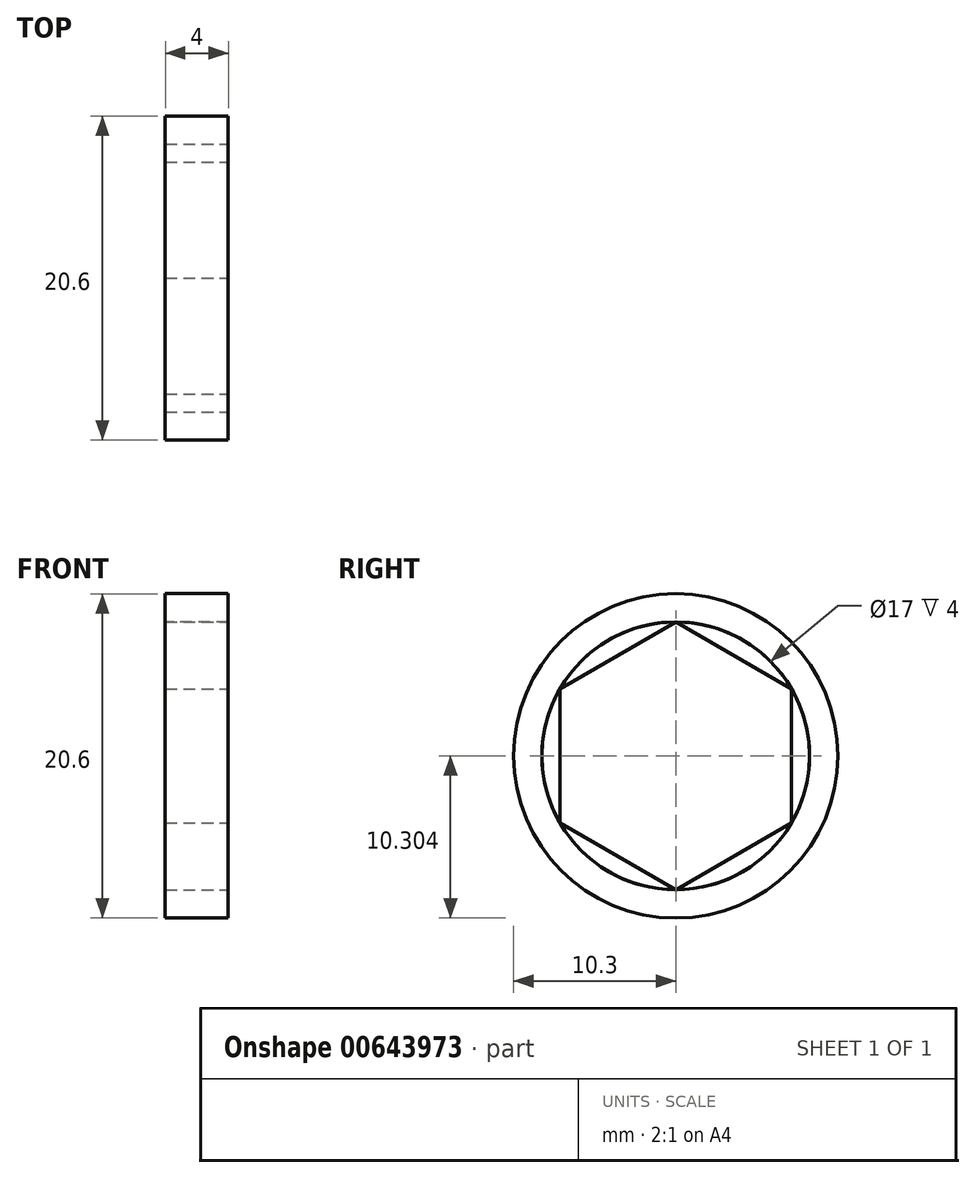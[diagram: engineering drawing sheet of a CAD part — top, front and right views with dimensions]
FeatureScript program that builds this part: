
annotation { "Feature Type Name" : "Feature", "Feature Type Description" : "" }
export const myFeature = defineFeature(function(context is Context, id is Id, definition is map)
    precondition{}
    {
        {
            var Q0;
            Q0=qCreatedBy(makeId("Front.planeOp"),FACE);
            var sketch = newSketch(context, id + "F0", { "sketchPlane" : qUnion([Q0])});
            skLineSegment(sketch, "E0.bottom", {"start": v(-21.35, 23.47) * mm, "end": v(-17.35, 23.47) * mm});
            skLineSegment(sketch, "E0.top", {"start": v(-21.35, 21.67) * mm, "end": v(-17.35, 21.67) * mm});
            skLineSegment(sketch, "E0.left", {"start": v(-21.35, 23.47) * mm, "end": v(-21.35, 21.67) * mm});
            skLineSegment(sketch, "E0.right", {"start": v(-17.35, 23.47) * mm, "end": v(-17.35, 21.67) * mm});
            skLineSegment(sketch, "E1", {"start": v(-28.05, 13.17) * mm, "end": v(-13.17, 13.17) * mm, "construction": true});
            skSolve(sketch);
        }
        {
            var Q0;
            Q0=makeQuery(id+"F0.imprint","IMPRINT",FACE,{"disambiguationData":[TD([[makeQuery(id+"F0.imprint","IMPRINT",EDGE,{"derivedFrom":sQuery(id+"F0.wireOp",EDGE,"E0.bottom")}),-1.0]])]});
            var Q1;
            Q1=sQuery(id+"F0.wireOp",EDGE,"E1");
            revolve(context, id + "F1", {"entities" : qUnion([Q0]), "axis" : qUnion([Q1]), "revolveType" : RevolveType.FULL});
        }
        {
            var Q0;
            Q0=makeQuery(id+"F1.opRevolve","SWEPT_FACE",FACE,{"disambiguationData":[OSD([sQuery(id+"F0.wireOp",EDGE,"E0.right")])]});
            var sketch = newSketch(context, id + "F2", { "sketchPlane" : qUnion([Q0])});
            skCircle(sketch, "E2.cCircle", {"center": v(0, 13.17) * mm, "radius": 8.5 * mm, "construction": true});
            skLineSegment(sketch, "E2.0", {"start": v(0, 21.67) * mm, "end": v(7.36, 17.42) * mm});
            skLineSegment(sketch, "E2.1", {"start": v(7.36, 17.42) * mm, "end": v(7.36, 8.92) * mm});
            skLineSegment(sketch, "E2.2", {"start": v(7.36, 8.92) * mm, "end": v(0, 4.67) * mm});
            skLineSegment(sketch, "E2.3", {"start": v(0, 4.67) * mm, "end": v(-7.36, 8.92) * mm});
            skLineSegment(sketch, "E2.4", {"start": v(-7.36, 8.92) * mm, "end": v(-7.36, 17.42) * mm});
            skLineSegment(sketch, "E2.5", {"start": v(-7.36, 17.42) * mm, "end": v(0, 21.67) * mm});
            skSolve(sketch);
        }
        {
            var Q0;
            {var subQ0=sQuery(id+"F2.wireOp",EDGE,"E2.5");Q0=makeQuery(id+"F2.imprint","IMPRINT",FACE,{"disambiguationData":[TD([[makeQuery(id+"F2.imprint","IMPRINT",EDGE,{"derivedFrom":subQ0}),1.0]])]});}
            var Q1;
            {var subQ0=sQuery(id+"F2.wireOp",EDGE,"E2.4");Q1=makeQuery(id+"F2.imprint","IMPRINT",FACE,{"disambiguationData":[TD([[makeQuery(id+"F2.imprint","IMPRINT",EDGE,{"derivedFrom":subQ0}),1.0]])]});}
            var Q2;
            {var subQ0=sQuery(id+"F2.wireOp",EDGE,"E2.3");Q2=makeQuery(id+"F2.imprint","IMPRINT",FACE,{"disambiguationData":[TD([[makeQuery(id+"F2.imprint","IMPRINT",EDGE,{"derivedFrom":subQ0}),1.0]])]});}
            var Q3;
            {var subQ0=sQuery(id+"F2.wireOp",EDGE,"E2.2");Q3=makeQuery(id+"F2.imprint","IMPRINT",FACE,{"disambiguationData":[TD([[makeQuery(id+"F2.imprint","IMPRINT",EDGE,{"derivedFrom":subQ0}),1.0]])]});}
            var Q4;
            {var subQ0=sQuery(id+"F2.wireOp",EDGE,"E2.1");Q4=makeQuery(id+"F2.imprint","IMPRINT",FACE,{"disambiguationData":[TD([[makeQuery(id+"F2.imprint","IMPRINT",EDGE,{"derivedFrom":subQ0}),1.0]])]});}
            var Q5;
            {var subQ0=sQuery(id+"F2.wireOp",EDGE,"E2.0");Q5=makeQuery(id+"F2.imprint","IMPRINT",FACE,{"disambiguationData":[TD([[makeQuery(id+"F2.imprint","IMPRINT",EDGE,{"derivedFrom":subQ0}),1.0]])]});}
            extrude(context, id + "F3", {"entities" : qUnion([Q0, Q1, Q2, Q3, Q4, Q5]), "oppositeDirection" : true, "depth" : 4 * mm, "offsetDistance" : 25 * mm});
        }
    });
